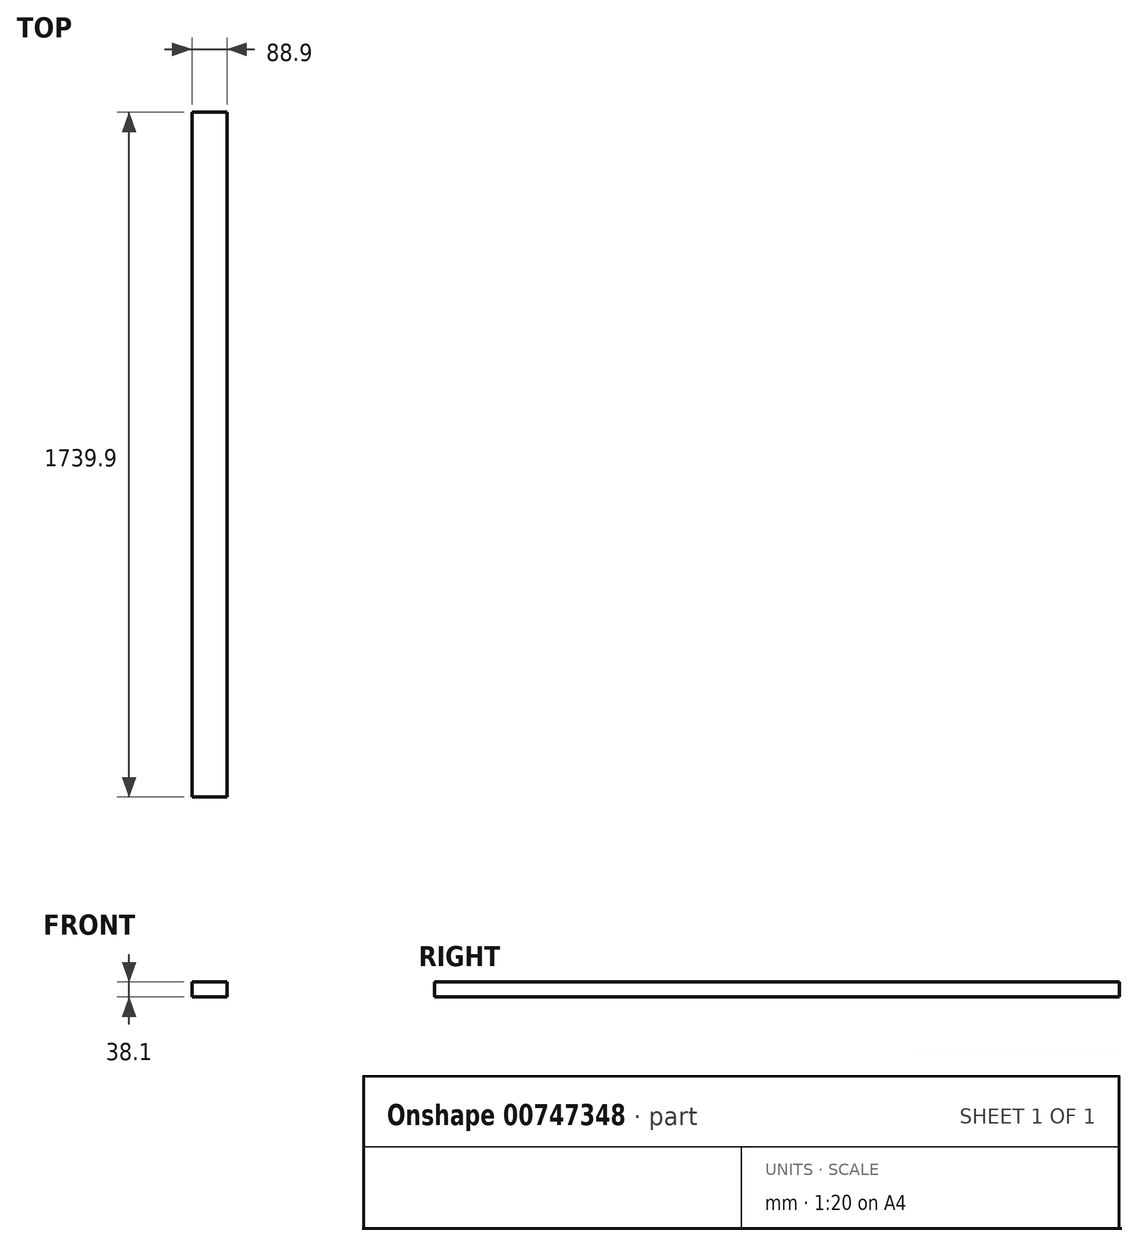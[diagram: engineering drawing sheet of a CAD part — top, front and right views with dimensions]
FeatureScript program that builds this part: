
annotation { "Feature Type Name" : "Feature", "Feature Type Description" : "" }
export const myFeature = defineFeature(function(context is Context, id is Id, definition is map)
    precondition{}
    {
        {
            var Q0;
            Q0=qCreatedBy(makeId("Front.planeOp"),FACE);
            var sketch = newSketch(context, id + "F0", { "sketchPlane" : qUnion([Q0])});
            skLineSegment(sketch, "E0.bottom", {"start": v(0, 0) * mm, "end": v(88.9, 0) * mm});
            skLineSegment(sketch, "E0.top", {"start": v(0, 38.1) * mm, "end": v(88.9, 38.1) * mm});
            skLineSegment(sketch, "E0.left", {"start": v(0, 0) * mm, "end": v(0, 38.1) * mm});
            skLineSegment(sketch, "E0.right", {"start": v(88.9, 0) * mm, "end": v(88.9, 38.1) * mm});
            skSolve(sketch);
        }
        {
            var Q0;
            Q0=qSketchRegion(id+"F0",true);
            extrude(context, id + "F1", {"entities" : qUnion([Q0]), "depth" : 1739.9 * mm, "offsetDistance" : 25.4 * mm});
        }
    });
